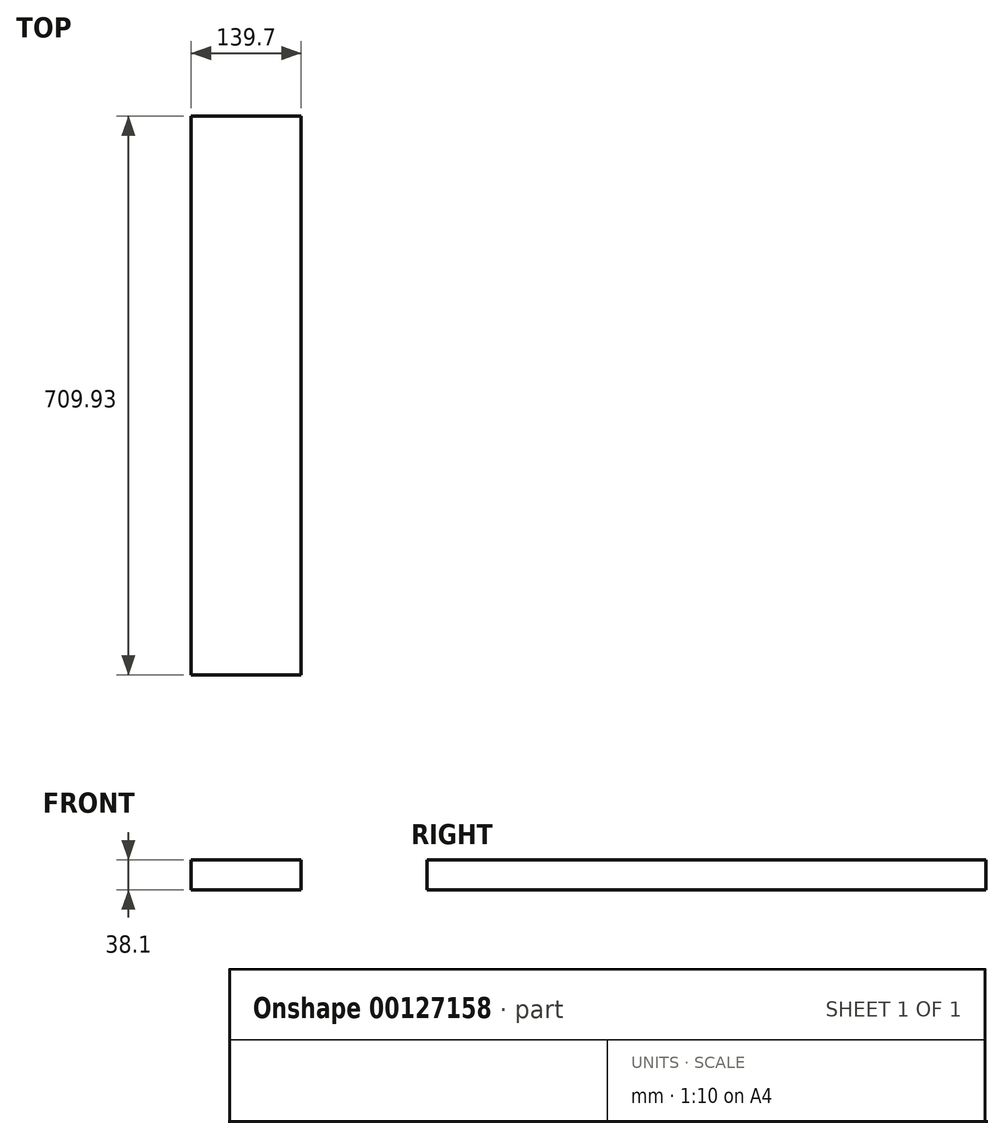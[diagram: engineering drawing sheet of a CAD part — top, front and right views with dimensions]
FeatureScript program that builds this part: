
annotation { "Feature Type Name" : "Feature", "Feature Type Description" : "" }
export const myFeature = defineFeature(function(context is Context, id is Id, definition is map)
    precondition{}
    {
        {
            var Q0;
            Q0=qCreatedBy(makeId("Front.planeOp"),FACE);
            var sketch = newSketch(context, id + "F0", { "sketchPlane" : qUnion([Q0])});
            skLineSegment(sketch, "E0.bottom", {"start": v(69.85, -19.05) * mm, "end": v(-69.85, -19.05) * mm});
            skLineSegment(sketch, "E0.top", {"start": v(69.85, 19.05) * mm, "end": v(-69.85, 19.05) * mm});
            skLineSegment(sketch, "E0.left", {"start": v(69.85, -19.05) * mm, "end": v(69.85, 19.05) * mm});
            skLineSegment(sketch, "E0.right", {"start": v(-69.85, -19.05) * mm, "end": v(-69.85, 19.05) * mm});
            skPoint(sketch, "E0.middle", {"position": v(0, 0) * mm});
            skSolve(sketch);
        }
        {
            var Q0;
            Q0=qSketchRegion(id+"F0",true);
            extrude(context, id + "F1", {"entities" : qUnion([Q0]), "depth" : 709.93 * mm, "offsetDistance" : 25.4 * mm});
        }
    });
